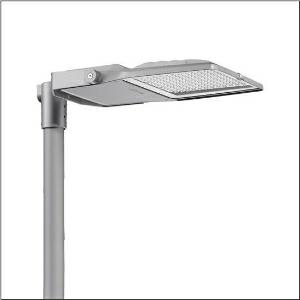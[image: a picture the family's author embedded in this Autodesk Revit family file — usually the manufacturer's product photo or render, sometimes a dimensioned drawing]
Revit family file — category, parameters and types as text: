
# Revit family: floodlight_fl_21_iq_midi___pl64_5xa7781f4e3a_1626
name_source: partatom
category: Lighting Fixtures
units: mm (PartAtom-declared; Revit-internal decimal feet)

## family parameters
Cut with Voids When Loaded = No
Host = Face
Light Source = No
Part Type = Normal
Room Calculation Point = No
Round Connector Dimension = Use Diameter
Shared = No

## types (1)
- --- (1 x LED, 36050 lm, 270.2 W, 4000K)
    Apparent Load = 270 VA
    CIE Flux Codes = 28 80 98 100 100
    Color Rendering = 70
    Color Temperature = 4000K
    Default Elevation = 1800 mm
    Description = Floodlight FL 21 iQ midi, floodlight, primary light control with lens, of PMMA, primary optical cover: protective disc, of toughened safety glass, transparent, light distribution: PL64, light emission: direct distribution, installation type: surface-mounted, LED, High Power LED, rated luminous flux: 36.050lm, luminous efficacy: 133lm/W, light colour: 740, colour temperature: 4000K, control gear: iQ Comfort/DALI, control: optimised constant luminous flux control (CLO 2.0), Desk-Remote (wireless, voltage-free reading and setting of iQ features in the workshop via application-optimized NFC function/RFID function), Light-Fading, Smart-Wire, Night-Set, Lumen-Switch, Temp-Guard, Auto-Match, with terminal, 6-pole, mains connection: 220..240V, AC, 50/60Hz, start of lifetime: 270W, end of service life: 287W, reduction: 118W, luminaire housing, of diecast aluminium, powder-coated, Siteco® metallic grey (DB 702S), corrosivity category C5 mid according to DIN EN ISO 12944, suitable for swimming pools, chlorine-resistant, sealing non-destructively replaceable, please order mast flange separately, mast bracket, of steel, galvanised, powder-coated, Siteco® metallic grey (DB 702S), protection rating (complete): IP66, insulation class (complete): insulation class II (safety insulation), certification: CE, ENEC, VDE, protection symbol: D, impact resistance: IK08, permissible operating ambient temperature: -40..+40°C, permissible operating ambient temperature for outdoor applications: -40..+50°C, standard: DIN EN 12944, LABS conformity tested according to VDMA 24364:2018-05, packaging unit: 1 piece

Light Distribution: PL64
    Height = 76 mm
    Lamp = 1 x LED
    Lamp Light Flux = 36050 lm
    Lamp Power = 270.2 W
    Lamp count = 1
    Length = 657 mm
    Luminous efficacy = 133 lm/W
    Manufacturer = Siteco
    ModVariant = No
    Model = 5XA7781F4E3A
    Number of Poles = 1
    OnlyDefault = Yes
    Power Factor = 1
    Product Name = Floodlight FL 21 iQ midi | PL64
    Product group = floodlight | pylon annexe
    ProductGroupID = 6200
    Protection Class = Protection class II
    Protection Degree = IP 66
    RLX_Detail_Level = 1
    RLX_Emergency_Light_Flux = 0 lm
    RLX_Emergency_Type = 0
    RLX_Emergency_Type_DB = No
    RlxData = <blob elided: 153753 chars, md5=c72c970e>
    Socket = socket
    Standby Power = 0 W
    System Light Flux = 36050 lm
    System Power = 270 W
    Type Comments = factory setting: luminous flux: 100 % | dim-lin: 254 | 620 mA
    Type Image = l_1007123.jpg
    URL = http://relux.com
    VarID = @adj_106792
    Voltage = 0 V
    Weight = 0.00 kg
    Width = 442 mm

## geometry (parser evidence)
native form markers: Blend x4, Sweep x12
no freeform markers — native parametric forms only
